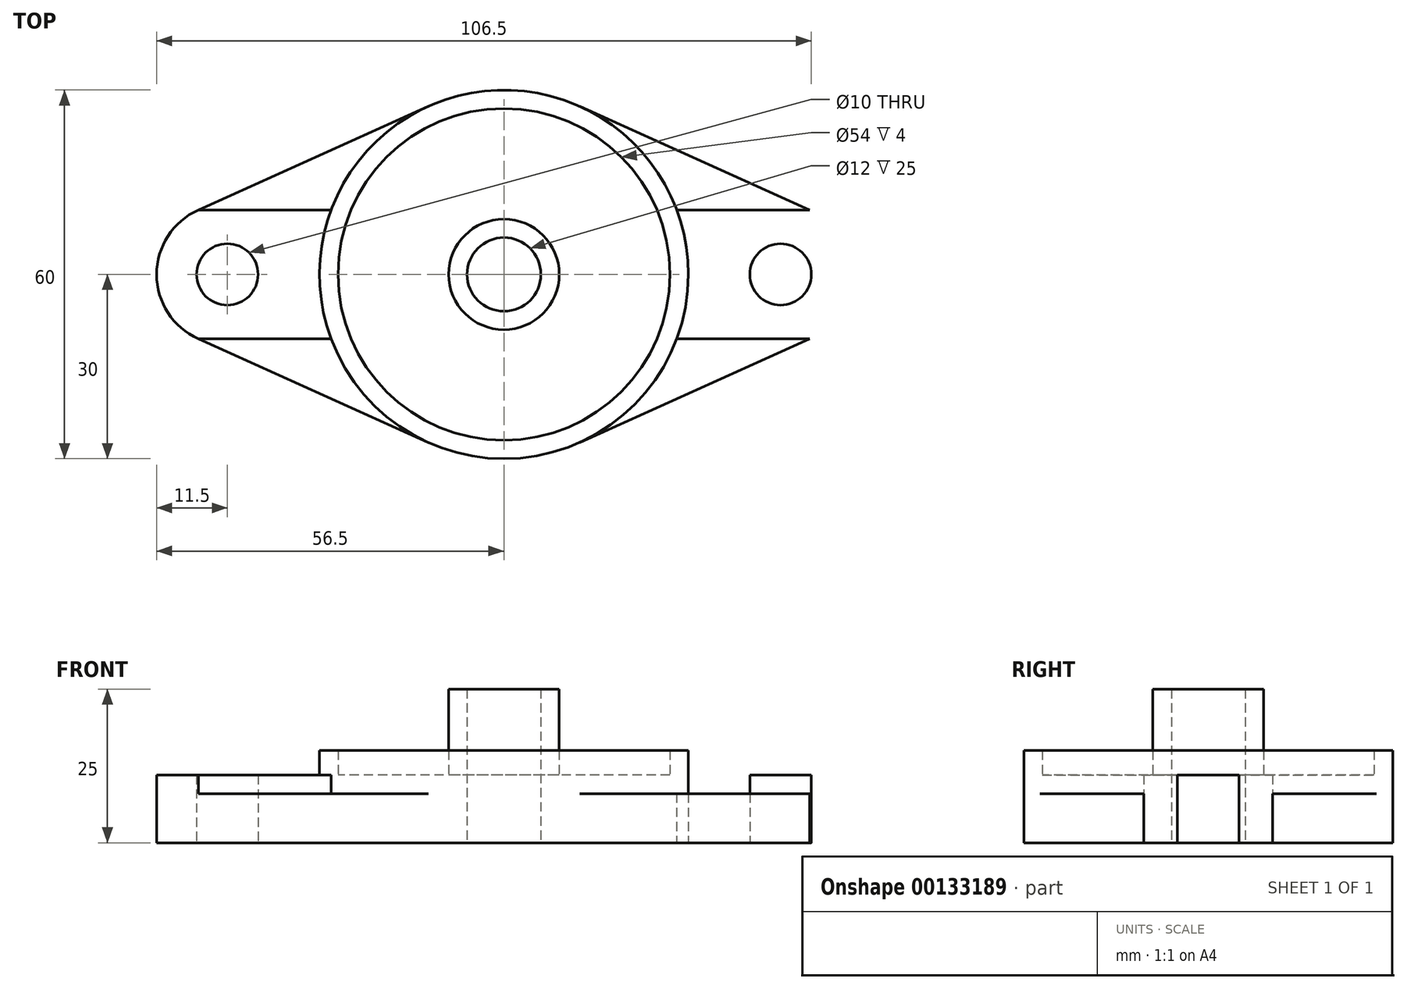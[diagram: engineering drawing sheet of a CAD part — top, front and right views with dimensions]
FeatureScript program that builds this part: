
annotation { "Feature Type Name" : "Feature", "Feature Type Description" : "" }
export const myFeature = defineFeature(function(context is Context, id is Id, definition is map)
    precondition{}
    {
        {
            var Q0;
            Q0=qCreatedBy(makeId("Top.planeOp"),FACE);
            var sketch = newSketch(context, id + "F0", { "sketchPlane" : qUnion([Q0])});
            skCircle(sketch, "E0", {"center": v(0, 0) * mm, "radius": 6 * mm});
            skCircle(sketch, "E1", {"center": v(0, 0) * mm, "radius": 30 * mm});
            skCircle(sketch, "E2.0", {"center": v(0, 0) * mm, "radius": 9 * mm});
            skCircle(sketch, "E3.0", {"center": v(0, 0) * mm, "radius": 27 * mm});
            skCircle(sketch, "E4", {"center": v(-45, 0) * mm, "radius": 5 * mm});
            skCircle(sketch, "E5.MirrorC", {"center": v(45, 0) * mm, "radius": 5 * mm});
            skArc(sketch, "E6", {"start": v(-49.73, 10.48) * mm, "mid": v(-56.5, 0) * mm, "end": v(-49.73, -10.48) * mm});
            skArc(sketch, "E7", {"start": v(49.73, -10.48) * mm, "mid": v(56.5, 0) * mm, "end": v(49.73, 10.48) * mm});
            skLineSegment(sketch, "E8", {"start": v(-49.73, 10.48) * mm, "end": v(-12.33, 27.35) * mm});
            skLineSegment(sketch, "E9", {"start": v(-49.73, -10.48) * mm, "end": v(-12.33, -27.35) * mm});
            skLineSegment(sketch, "E10", {"start": v(-49.73, 10.48) * mm, "end": v(-28.1, 10.48) * mm});
            skLineSegment(sketch, "E11", {"start": v(-49.73, -10.48) * mm, "end": v(-28.1, -10.48) * mm});
            skLineSegment(sketch, "E12", {"start": v(12.33, 27.35) * mm, "end": v(49.73, 10.48) * mm});
            skLineSegment(sketch, "E13", {"start": v(49.73, -10.48) * mm, "end": v(12.33, -27.35) * mm});
            skLineSegment(sketch, "E14", {"start": v(49.73, -10.48) * mm, "end": v(28.1, -10.48) * mm});
            skLineSegment(sketch, "E15", {"start": v(49.73, 10.48) * mm, "end": v(28.1, 10.48) * mm});
            skSolve(sketch);
        }
        {
            var Q0;
            Q0=makeQuery(id+"F0.imprint","IMPRINT",FACE,{"disambiguationData":[TD([[makeQuery(id+"F0.imprint","IMPRINT",EDGE,{"derivedFrom":sQuery(id+"F0.wireOp",EDGE,"E4")}),-1.0]])]});
            var Q1;
            Q1=makeQuery(id+"F0.imprint","IMPRINT",FACE,{"disambiguationData":[TD([[makeQuery(id+"F0.imprint","IMPRINT",EDGE,{"derivedFrom":sQuery(id+"F0.wireOp",EDGE,"E5.MirrorC")}),1.0]])]});
            extrude(context, id + "F1", {"entities" : qUnion([Q0, Q1]), "depth" : 11 * mm});
        }
        {
            var Q0;
            Q0=makeQuery(id+"F0.imprint","IMPRINT",FACE,{"disambiguationData":[TD([[makeQuery(id+"F0.imprint","IMPRINT",EDGE,{"derivedFrom":sQuery(id+"F0.wireOp",EDGE,"E3.0")}),-1.0]])]});
            extrude(context, id + "F2", {"entities" : qUnion([Q0]), "operationType" : NewBodyOperationType.ADD, "depth" : 15 * mm});
        }
        {
            var Q0;
            Q0=makeQuery(id+"F0.imprint","IMPRINT",FACE,{"disambiguationData":[TD([[makeQuery(id+"F0.imprint","IMPRINT",EDGE,{"derivedFrom":sQuery(id+"F0.wireOp",EDGE,"E2.0")}),-1.0]])]});
            extrude(context, id + "F3", {"entities" : qUnion([Q0]), "operationType" : NewBodyOperationType.ADD, "depth" : 11 * mm});
        }
        {
            var Q0;
            Q0=makeQuery(id+"F0.imprint","IMPRINT",FACE,{"disambiguationData":[TD([[makeQuery(id+"F0.imprint","IMPRINT",EDGE,{"derivedFrom":sQuery(id+"F0.wireOp",EDGE,"E0")}),-1.0]])]});
            extrude(context, id + "F4", {"entities" : qUnion([Q0]), "operationType" : NewBodyOperationType.ADD, "depth" : 25 * mm});
        }
        {
            var Q0;
            {var subQ0=sQuery(id+"F0.wireOp",EDGE,"E9");Q0=makeQuery(id+"F0.imprint","IMPRINT",FACE,{"disambiguationData":[TD([[makeQuery(id+"F0.imprint","IMPRINT",EDGE,{"derivedFrom":subQ0}),1.0]])]});}
            var Q1;
            {var subQ0=sQuery(id+"F0.wireOp",EDGE,"E13");Q1=makeQuery(id+"F0.imprint","IMPRINT",FACE,{"disambiguationData":[TD([[makeQuery(id+"F0.imprint","IMPRINT",EDGE,{"derivedFrom":subQ0}),-1.0]])]});}
            var Q2;
            {var subQ0=sQuery(id+"F0.wireOp",EDGE,"E8");Q2=makeQuery(id+"F0.imprint","IMPRINT",FACE,{"disambiguationData":[TD([[makeQuery(id+"F0.imprint","IMPRINT",EDGE,{"derivedFrom":subQ0}),-1.0]])]});}
            var Q3;
            {var subQ0=sQuery(id+"F0.wireOp",EDGE,"E12");Q3=makeQuery(id+"F0.imprint","IMPRINT",FACE,{"disambiguationData":[TD([[makeQuery(id+"F0.imprint","IMPRINT",EDGE,{"derivedFrom":subQ0}),-1.0]])]});}
            extrude(context, id + "F5", {"entities" : qUnion([Q0, Q1, Q2, Q3]), "operationType" : NewBodyOperationType.ADD, "depth" : 8 * mm});
        }
    });
